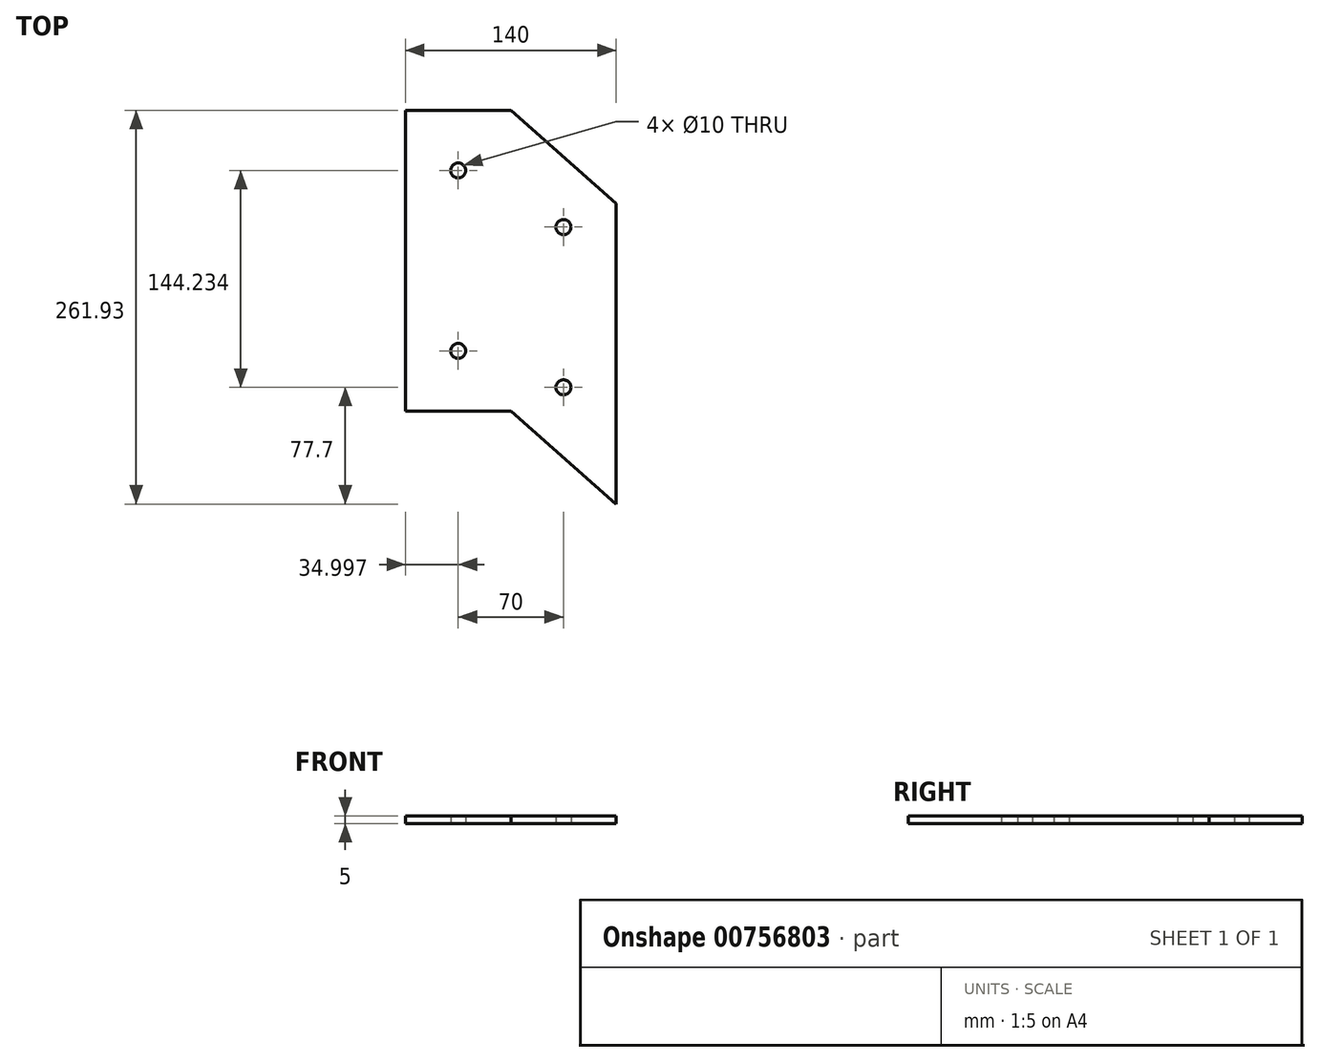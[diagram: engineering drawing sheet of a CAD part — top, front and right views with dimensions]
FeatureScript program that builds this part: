
annotation { "Feature Type Name" : "Feature", "Feature Type Description" : "" }
export const myFeature = defineFeature(function(context is Context, id is Id, definition is map)
    precondition{}
    {
        {
            var Q0;
            Q0=qCreatedBy(makeId("Top.planeOp"), FACE);
            var sketch = newSketch(context, id + "F0", { "sketchPlane" : qUnion([Q0])});
            skLineSegment(sketch, "E0.bottom", {"start": v(-83.95, 184.23) * mm, "end": v(-13.95, 184.23) * mm});
            skLineSegment(sketch, "E0.top", {"start": v(-83.95, -15.77) * mm, "end": v(-13.95, -15.77) * mm});
            skLineSegment(sketch, "E0.left", {"start": v(-83.95, 184.23) * mm, "end": v(-83.95, -15.77) * mm});
            skLineSegment(sketch, "E0.right", {"start": v(-13.95, 184.23) * mm, "end": v(-13.95, -15.77) * mm});
            skLineSegment(sketch, "E1", {"start": v(-13.95, 184.23) * mm, "end": v(56.05, 122.3) * mm});
            skLineSegment(sketch, "E2", {"start": v(56.05, 122.3) * mm, "end": v(56.05, -77.7) * mm});
            skLineSegment(sketch, "E3", {"start": v(56.05, -77.7) * mm, "end": v(-13.95, -15.77) * mm});
            skCircle(sketch, "E4", {"center": v(-48.95, 144.23) * mm, "radius": 5 * mm});
            skCircle(sketch, "E5", {"center": v(-48.95, 24.23) * mm, "radius": 5 * mm});
            skCircle(sketch, "E6", {"center": v(21.05, 106.54) * mm, "radius": 5 * mm});
            skCircle(sketch, "E7", {"center": v(21.05, 0) * mm, "radius": 5 * mm});
            skSolve(sketch);
        }
        {
            var Q0;
            Q0 = qSketchRegion(id + "F0", true);
            extrude(context, id + "F1", {"entities" : qUnion([Q0]), "depth" : 5 * mm, "offsetDistance" : 25 * mm});
        }
    });
